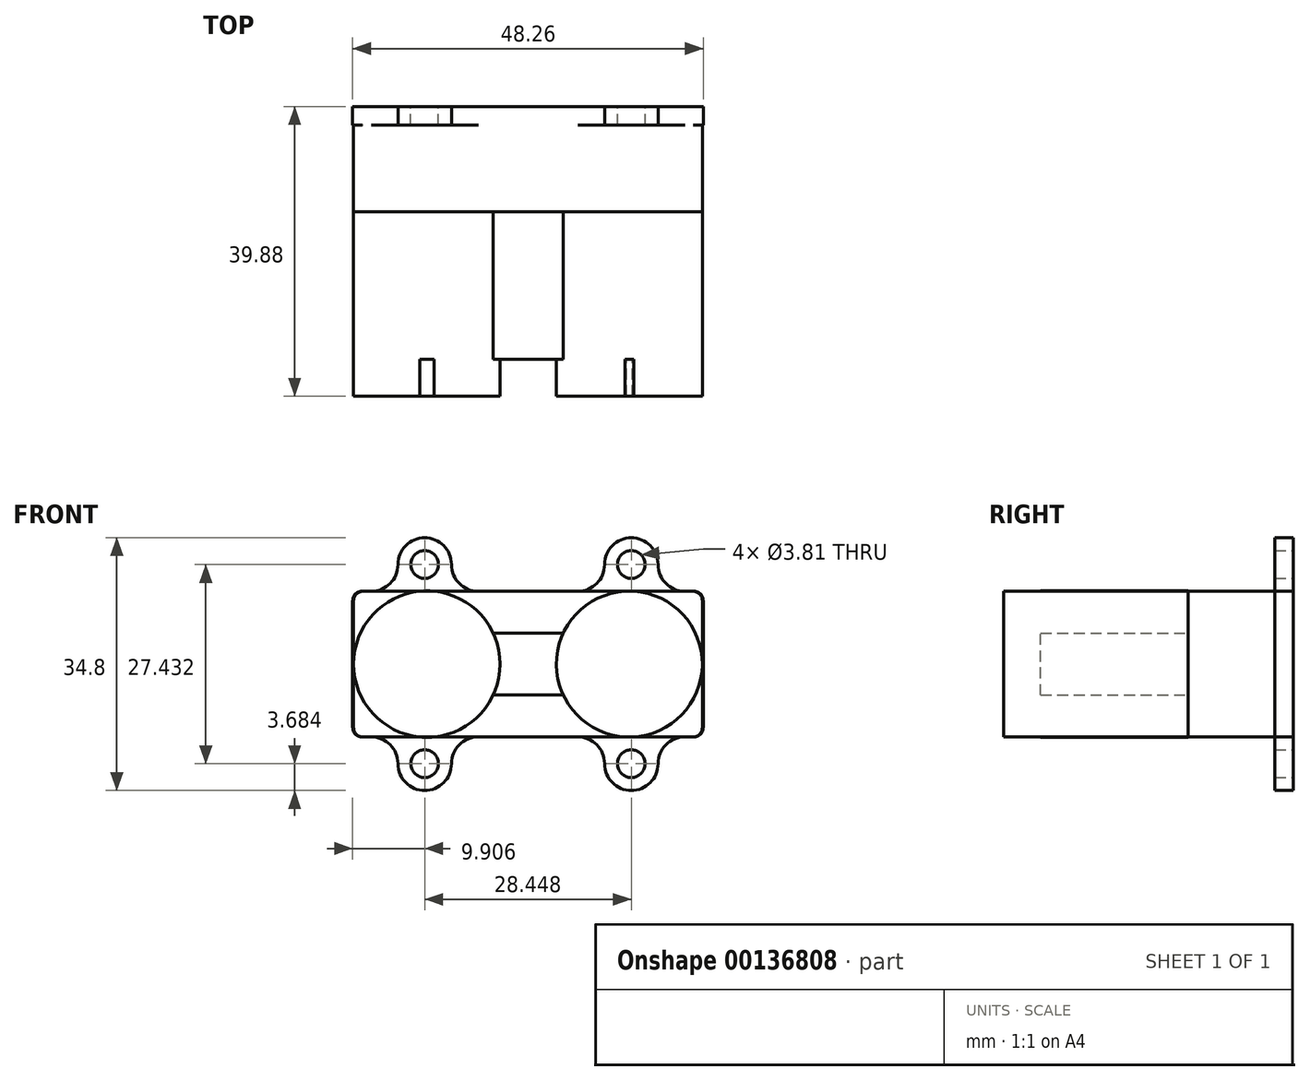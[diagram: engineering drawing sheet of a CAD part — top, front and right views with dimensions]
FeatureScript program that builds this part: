
annotation { "Feature Type Name" : "Feature", "Feature Type Description" : "" }
export const myFeature = defineFeature(function(context is Context, id is Id, definition is map)
    precondition{}
    {
        {
            var Q0;
            Q0=qCreatedBy(makeId("Front.planeOp"),FACE);
            var sketch = newSketch(context, id + "F0", { "sketchPlane" : qUnion([Q0])});
            skLineSegment(sketch, "E0.bottom", {"start": v(22.86, 10.03) * mm, "end": v(-22.86, 10.03) * mm});
            skLineSegment(sketch, "E0.top", {"start": v(22.86, -10.03) * mm, "end": v(-22.86, -10.03) * mm});
            skLineSegment(sketch, "E0.left", {"start": v(24.13, 8.76) * mm, "end": v(24.13, -8.76) * mm});
            skLineSegment(sketch, "E0.right", {"start": v(-24.13, 8.76) * mm, "end": v(-24.13, -8.76) * mm});
            skPoint(sketch, "E0.middle", {"position": v(0, 0) * mm});
            skCircle(sketch, "E1", {"center": v(-14.22, 13.72) * mm, "radius": 1.9 * mm});
            skCircle(sketch, "E2", {"center": v(-14.22, 13.72) * mm, "radius": 3.68 * mm});
            skPoint(sketch, "E3.visualSharp", {"position": v(24.13, 10.03) * mm});
            skArc(sketch, "E3.filletArc", {"start": v(24.13, 8.76) * mm, "mid": v(23.76, 9.66) * mm, "end": v(22.86, 10.03) * mm});
            skPoint(sketch, "E4.visualSharp", {"position": v(24.13, -10.03) * mm});
            skArc(sketch, "E4.filletArc", {"start": v(22.86, -10.03) * mm, "mid": v(23.76, -9.66) * mm, "end": v(24.13, -8.76) * mm});
            skPoint(sketch, "E5.visualSharp", {"position": v(-24.13, -10.03) * mm});
            skArc(sketch, "E5.filletArc", {"start": v(-24.13, -8.76) * mm, "mid": v(-23.76, -9.66) * mm, "end": v(-22.86, -10.03) * mm});
            skPoint(sketch, "E6.visualSharp", {"position": v(-24.13, 10.03) * mm});
            skArc(sketch, "E6.filletArc", {"start": v(-22.86, 10.03) * mm, "mid": v(-23.76, 9.66) * mm, "end": v(-24.13, 8.76) * mm});
            skArc(sketch, "E7", {"start": v(-10.54, 13.72) * mm, "mid": v(-9.46, 11.11) * mm, "end": v(-6.86, 10.03) * mm});
            skArc(sketch, "E8", {"start": v(-21.6, 10.03) * mm, "mid": v(-18.99, 11.11) * mm, "end": v(-17.9, 13.72) * mm});
            skCircle(sketch, "E9.MirrorC", {"center": v(14.22, 13.72) * mm, "radius": 1.9 * mm});
            skCircle(sketch, "E10.MirrorC", {"center": v(14.22, 13.72) * mm, "radius": 3.68 * mm});
            skArc(sketch, "E11.MirrorCS", {"start": v(10.54, 13.72) * mm, "mid": v(9.46, 11.11) * mm, "end": v(6.86, 10.03) * mm});
            skArc(sketch, "E12.MirrorCS", {"start": v(21.6, 10.03) * mm, "mid": v(18.99, 11.11) * mm, "end": v(17.9, 13.72) * mm});
            skArc(sketch, "E13.MirrorCS", {"start": v(-21.6, -10.03) * mm, "mid": v(-18.99, -11.11) * mm, "end": v(-17.9, -13.72) * mm});
            skCircle(sketch, "E14.MirrorC", {"center": v(-14.22, -13.72) * mm, "radius": 3.68 * mm});
            skCircle(sketch, "E15.MirrorC", {"center": v(-14.22, -13.72) * mm, "radius": 1.9 * mm});
            skArc(sketch, "E16.MirrorCS", {"start": v(-10.54, -13.72) * mm, "mid": v(-9.46, -11.11) * mm, "end": v(-6.86, -10.03) * mm});
            skArc(sketch, "E17.MirrorCS", {"start": v(10.54, -13.72) * mm, "mid": v(9.46, -11.11) * mm, "end": v(6.86, -10.03) * mm});
            skCircle(sketch, "E18.MirrorC", {"center": v(14.22, -13.72) * mm, "radius": 3.68 * mm});
            skCircle(sketch, "E19.MirrorC", {"center": v(14.22, -13.72) * mm, "radius": 1.9 * mm});
            skArc(sketch, "E20.MirrorCS", {"start": v(21.6, -10.03) * mm, "mid": v(18.99, -11.11) * mm, "end": v(17.9, -13.72) * mm});
            skSolve(sketch);
        }
        {
            var Q0;
            Q0 = qSketchRegion(id + "F0", true);
            extrude(context, id + "F1", {"entities" : qUnion([Q0]), "endBound" : BoundingType.SYMMETRIC, "depth" : 2.54 * mm});
        }
        {
            var Q0;
            Q0=makeQuery(id+"F1.opExtrude","CAP_FACE",FACE,{"disambiguationData":[OSD([sQuery(id+"F0.wireOp",EDGE,"E0.bottom"),sQuery(id+"F0.wireOp",EDGE,"E0.top"),sQuery(id+"F0.wireOp",EDGE,"E0.left"),sQuery(id+"F0.wireOp",EDGE,"E0.right"),sQuery(id+"F0.wireOp",EDGE,"E1"),sQuery(id+"F0.wireOp",EDGE,"E2"),sQuery(id+"F0.wireOp",EDGE,"E3.filletArc"),sQuery(id+"F0.wireOp",EDGE,"E4.filletArc"),sQuery(id+"F0.wireOp",EDGE,"E5.filletArc"),sQuery(id+"F0.wireOp",EDGE,"E6.filletArc"),sQuery(id+"F0.wireOp",EDGE,"E7"),sQuery(id+"F0.wireOp",EDGE,"E8"),sQuery(id+"F0.wireOp",EDGE,"E9.MirrorC"),sQuery(id+"F0.wireOp",EDGE,"E10.MirrorC"),sQuery(id+"F0.wireOp",EDGE,"E11.MirrorCS"),sQuery(id+"F0.wireOp",EDGE,"E12.MirrorCS"),sQuery(id+"F0.wireOp",EDGE,"E13.MirrorCS"),sQuery(id+"F0.wireOp",EDGE,"E14.MirrorC"),sQuery(id+"F0.wireOp",EDGE,"E15.MirrorC"),sQuery(id+"F0.wireOp",EDGE,"E16.MirrorCS"),sQuery(id+"F0.wireOp",EDGE,"E17.MirrorCS"),sQuery(id+"F0.wireOp",EDGE,"E18.MirrorC"),sQuery(id+"F0.wireOp",EDGE,"E19.MirrorC"),sQuery(id+"F0.wireOp",EDGE,"E20.MirrorCS")])],"isStart":false});
            var sketch = newSketch(context, id + "F2", { "sketchPlane" : qUnion([Q0])});
            skLineSegment(sketch, "E21.bottom", {"start": v(22.73, 10.03) * mm, "end": v(-22.73, 10.03) * mm});
            skLineSegment(sketch, "E21.top", {"start": v(22.73, -10.03) * mm, "end": v(-22.73, -10.03) * mm});
            skLineSegment(sketch, "E21.left", {"start": v(24, 8.76) * mm, "end": v(24, -8.76) * mm});
            skLineSegment(sketch, "E21.right", {"start": v(-24, 8.76) * mm, "end": v(-24, -8.76) * mm});
            skPoint(sketch, "E21.middle", {"position": v(0, 0) * mm});
            skPoint(sketch, "E22.visualSharp", {"position": v(-24, 10.03) * mm});
            skArc(sketch, "E22.filletArc", {"start": v(-22.73, 10.03) * mm, "mid": v(-23.63, 9.66) * mm, "end": v(-24, 8.76) * mm});
            skPoint(sketch, "E23.visualSharp", {"position": v(24, 10.03) * mm});
            skArc(sketch, "E23.filletArc", {"start": v(24, 8.76) * mm, "mid": v(23.63, 9.66) * mm, "end": v(22.73, 10.03) * mm});
            skPoint(sketch, "E24.visualSharp", {"position": v(-24, -10.03) * mm});
            skArc(sketch, "E24.filletArc", {"start": v(-24, -8.76) * mm, "mid": v(-23.63, -9.66) * mm, "end": v(-22.73, -10.03) * mm});
            skPoint(sketch, "E25.visualSharp", {"position": v(24, -10.03) * mm});
            skArc(sketch, "E25.filletArc", {"start": v(22.73, -10.03) * mm, "mid": v(23.63, -9.66) * mm, "end": v(24, -8.76) * mm});
            skSolve(sketch);
        }
        {
            var Q0;
            Q0 = qSketchRegion(id + "F2", true);
            extrude(context, id + "F3", {"entities" : qUnion([Q0]), "operationType" : NewBodyOperationType.ADD, "depth" : 11.94 * mm});
        }
        {
            var Q0;
            Q0=makeQuery(id+"F3.opExtrude","CAP_FACE",FACE,{"disambiguationData":[OSD([sQuery(id+"F2.wireOp",EDGE,"E21.bottom"),sQuery(id+"F2.wireOp",EDGE,"E21.top"),sQuery(id+"F2.wireOp",EDGE,"E21.left"),sQuery(id+"F2.wireOp",EDGE,"E21.right"),sQuery(id+"F2.wireOp",EDGE,"E22.filletArc"),sQuery(id+"F2.wireOp",EDGE,"E23.filletArc"),sQuery(id+"F2.wireOp",EDGE,"E24.filletArc"),sQuery(id+"F2.wireOp",EDGE,"E25.filletArc")])],"isStart":false});
            var sketch = newSketch(context, id + "F4", { "sketchPlane" : qUnion([Q0])});
            skCircle(sketch, "E26", {"center": v(-13.92, 0) * mm, "radius": 10.08 * mm});
            skPoint(sketch, "E26.first.point", {"position": v(-24, 0) * mm});
            skPoint(sketch, "E26.second.point", {"position": v(-12.94, 10.03) * mm});
            skPoint(sketch, "E26.third.point", {"position": v(-12.94, -10.03) * mm});
            skCircle(sketch, "E27", {"center": v(13.96, 0) * mm, "radius": 10.05 * mm});
            skPoint(sketch, "E27.first.point", {"position": v(14.57, 10.03) * mm});
            skPoint(sketch, "E27.second.point", {"position": v(24, 0) * mm});
            skPoint(sketch, "E27.third.point", {"position": v(13.53, -10.03) * mm});
            skLineSegment(sketch, "E28.bottom", {"start": v(13.96, 4.25) * mm, "end": v(-13.96, 4.25) * mm});
            skLineSegment(sketch, "E28.top", {"start": v(13.96, -4.25) * mm, "end": v(-13.96, -4.25) * mm});
            skLineSegment(sketch, "E28.left", {"start": v(13.96, 4.25) * mm, "end": v(13.96, -4.25) * mm});
            skLineSegment(sketch, "E28.right", {"start": v(-13.96, 4.25) * mm, "end": v(-13.96, -4.25) * mm});
            skPoint(sketch, "E28.middle", {"position": v(0, 0) * mm});
            skSolve(sketch);
        }
        {
            var Q0;
            {var subQ5=sQuery(id+"F4.wireOp",EDGE,"E28.left");Q0=makeQuery(id+"F4.imprint","IMPRINT",FACE,{"disambiguationData":[TD([[makeQuery(id+"F4.imprint","IMPRINT",EDGE,{"derivedFrom":subQ5}),-1.0]])]});}
            var Q1;
            {var subQ10=sQuery(id+"F4.wireOp",EDGE,"E28.left");Q1=makeQuery(id+"F4.imprint","IMPRINT",FACE,{"disambiguationData":[TD([[makeQuery(id+"F4.imprint","IMPRINT",EDGE,{"derivedFrom":subQ10}),1.0]])]});}
            var Q2;
            {var subQ5=sQuery(id+"F4.wireOp",EDGE,"E28.right");Q2=makeQuery(id+"F4.imprint","IMPRINT",FACE,{"disambiguationData":[TD([[makeQuery(id+"F4.imprint","IMPRINT",EDGE,{"derivedFrom":subQ5}),1.0]])]});}
            var Q3;
            {var subQ9=sQuery(id+"F4.wireOp",EDGE,"E28.right");Q3=makeQuery(id+"F4.imprint","IMPRINT",FACE,{"disambiguationData":[TD([[makeQuery(id+"F4.imprint","IMPRINT",EDGE,{"derivedFrom":subQ9}),-1.0]])]});}
            extrude(context, id + "F5", {"entities" : qUnion([Q0, Q1, Q2, Q3]), "operationType" : NewBodyOperationType.ADD, "depth" : 25.4 * mm});
        }
        {
            var Q0;
            Q0 = qSketchRegion(id + "F4", true);
            extrude(context, id + "F6", {"entities" : qUnion([Q0]), "operationType" : NewBodyOperationType.ADD, "depth" : 20.32 * mm});
        }
    });
